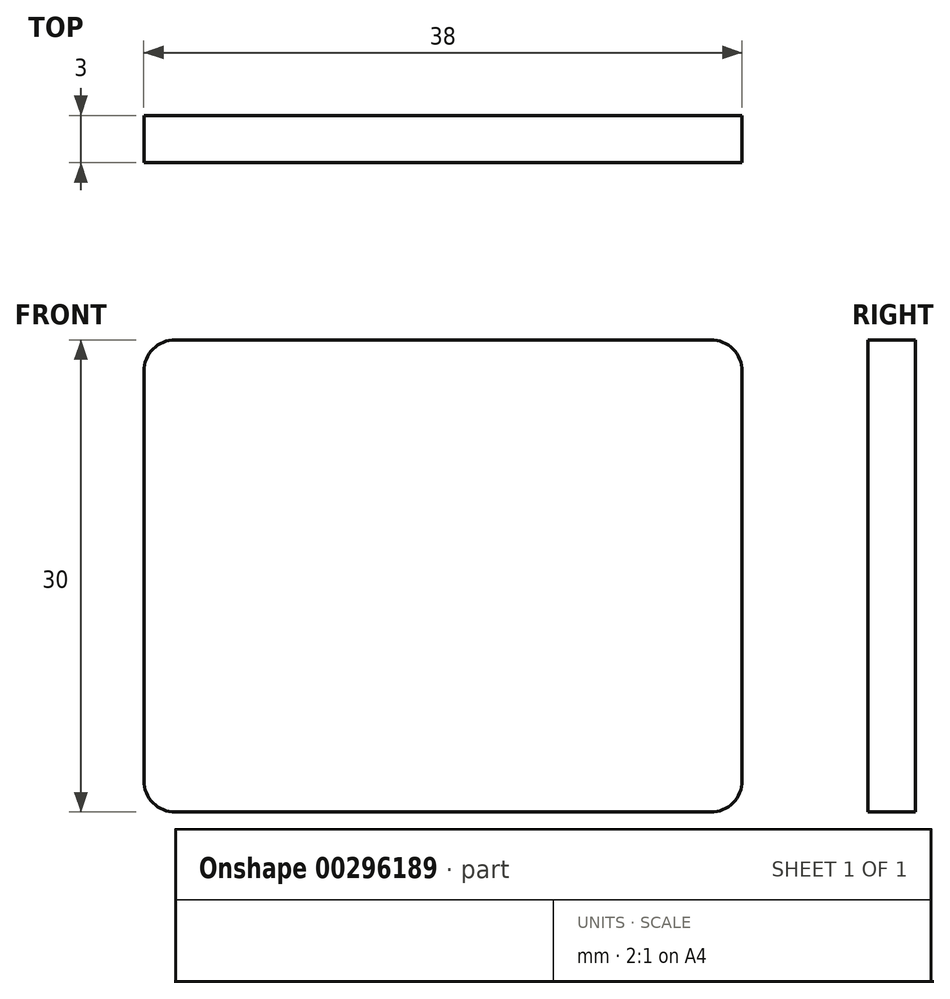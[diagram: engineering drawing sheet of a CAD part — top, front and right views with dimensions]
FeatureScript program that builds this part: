
annotation { "Feature Type Name" : "Feature", "Feature Type Description" : "" }
export const myFeature = defineFeature(function(context is Context, id is Id, definition is map)
    precondition{}
    {
        {
            var Q0;
            Q0=qCreatedBy(makeId("Front.planeOp"),FACE);
            var sketch = newSketch(context, id + "F0", { "sketchPlane" : qUnion([Q0])});
            skLineSegment(sketch, "E0.bottom", {"start": v(-16.86, 21.87) * mm, "end": v(17.14, 21.87) * mm});
            skLineSegment(sketch, "E0.top", {"start": v(-16.86, -8.13) * mm, "end": v(17.14, -8.13) * mm});
            skLineSegment(sketch, "E0.left", {"start": v(-18.86, 19.87) * mm, "end": v(-18.86, -6.13) * mm});
            skLineSegment(sketch, "E0.right", {"start": v(19.14, 19.87) * mm, "end": v(19.14, -6.13) * mm});
            skPoint(sketch, "E1.visualSharp", {"position": v(19.14, 21.87) * mm});
            skArc(sketch, "E1.filletArc", {"start": v(19.14, 19.87) * mm, "mid": v(18.56, 21.28) * mm, "end": v(17.14, 21.87) * mm});
            skPoint(sketch, "E2.visualSharp", {"position": v(-18.86, 21.87) * mm});
            skArc(sketch, "E2.filletArc", {"start": v(-16.86, 21.87) * mm, "mid": v(-18.27, 21.28) * mm, "end": v(-18.86, 19.87) * mm});
            skArc(sketch, "E3.filletArc", {"start": v(-18.86, -6.13) * mm, "mid": v(-18.27, -7.55) * mm, "end": v(-16.86, -8.13) * mm});
            skPoint(sketch, "E4.visualSharp", {"position": v(19.14, -8.13) * mm});
            skArc(sketch, "E4.filletArc", {"start": v(17.14, -8.13) * mm, "mid": v(18.56, -7.55) * mm, "end": v(19.14, -6.13) * mm});
            skSolve(sketch);
        }
        {
            var Q0;
            Q0 = qSketchRegion(id + "F0", true);
            extrude(context, id + "F1", {"entities" : qUnion([Q0]), "depth" : 3 * mm});
        }
    });
